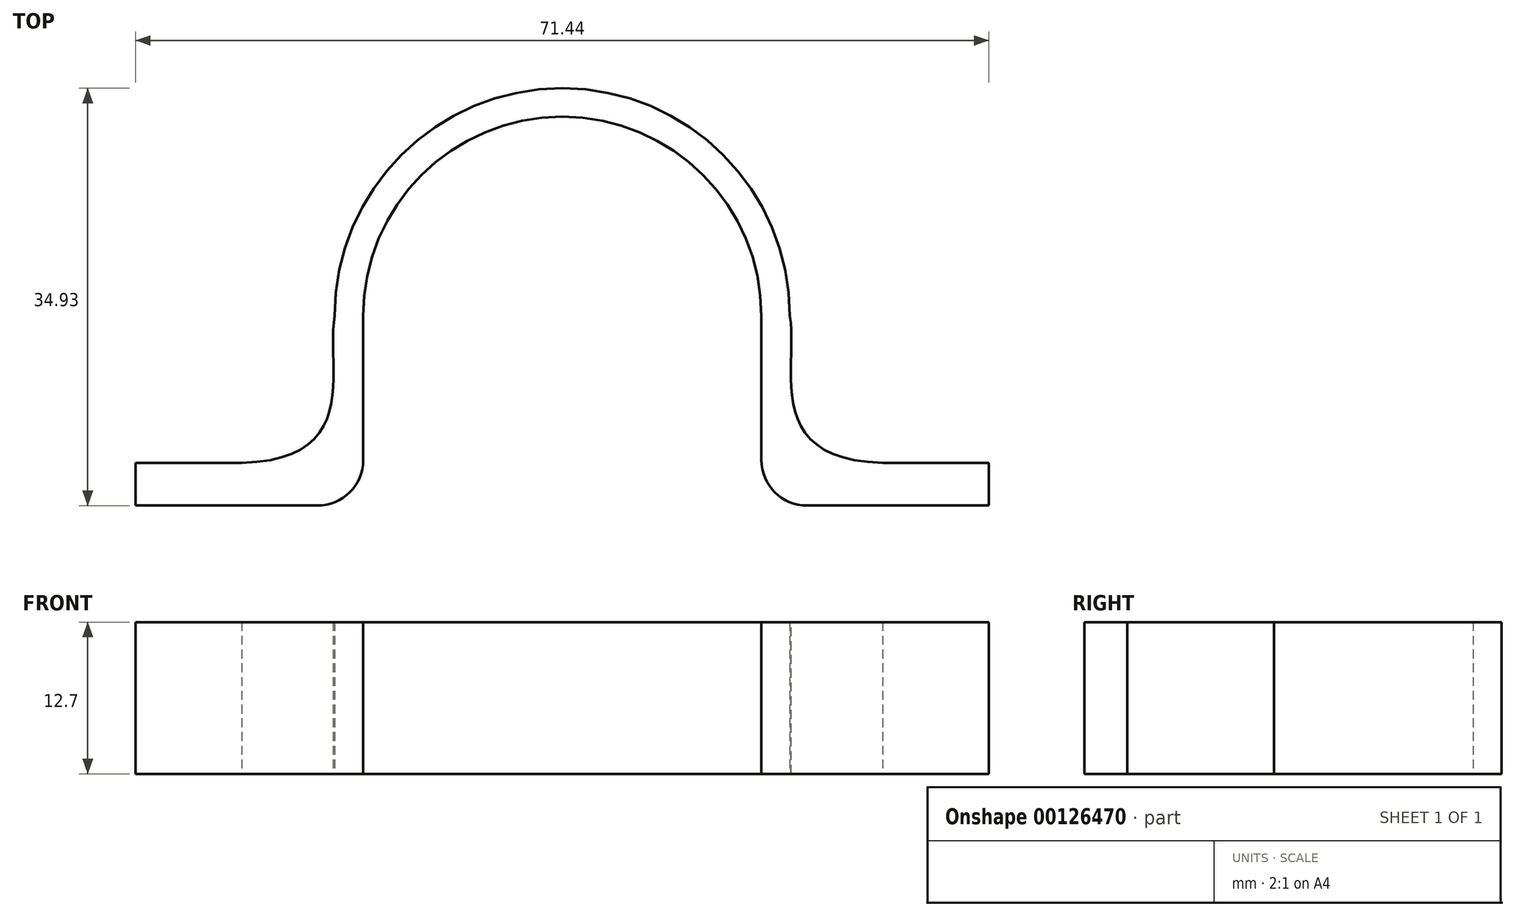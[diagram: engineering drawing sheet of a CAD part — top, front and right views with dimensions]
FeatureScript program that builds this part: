
annotation { "Feature Type Name" : "Feature", "Feature Type Description" : "" }
export const myFeature = defineFeature(function(context is Context, id is Id, definition is map)
    precondition{}
    {
        {
            var Q0;
            Q0=qCreatedBy(makeId("Top.planeOp"),FACE);
            var sketch = newSketch(context, id + "F0", { "sketchPlane" : qUnion([Q0])});
            skCircle(sketch, "E0", {"center": v(0, 0) * mm, "radius": 15.88 * mm, "construction": true});
            skCircle(sketch, "E1", {"center": v(0, 0) * mm, "radius": 16.67 * mm, "construction": true});
            skArc(sketch, "E2", {"start": v(16.67, 0) * mm, "mid": v(11.79, 11.79) * mm, "end": v(0, 16.67) * mm});
            skPoint(sketch, "E3", {"position": v(0, -15.88) * mm});
            skLineSegment(sketch, "E4", {"start": v(16.67, 0) * mm, "end": v(16.67, -12.06) * mm});
            skPoint(sketch, "E5", {"position": v(0, 16.67) * mm});
            skPoint(sketch, "E6", {"position": v(16.67, -15.88) * mm});
            skCircle(sketch, "E7", {"center": v(0, 0) * mm, "radius": 19.05 * mm, "construction": true});
            skLineSegment(sketch, "E8", {"start": v(20.48, -15.88) * mm, "end": v(35.72, -15.88) * mm});
            skArc(sketch, "E9.filletArc", {"start": v(16.67, -12.06) * mm, "mid": v(17.78, -14.76) * mm, "end": v(20.48, -15.87) * mm});
            skPoint(sketch, "E10", {"position": v(0, 19.05) * mm});
            skArc(sketch, "E11", {"start": v(19.05, 0) * mm, "mid": v(13.47, 13.47) * mm, "end": v(0, 19.05) * mm});
            skLineSegment(sketch, "E12", {"start": v(26.82, -12.3) * mm, "end": v(35.72, -12.3) * mm});
            skLineSegment(sketch, "E13", {"start": v(35.72, -12.3) * mm, "end": v(35.72, -15.88) * mm});
            skLineSegment(sketch, "E14", {"start": v(0, 0) * mm, "end": v(0, 19.05) * mm, "construction": true});
            skFitSpline(sketch, "E15", {"points": [v(19.05, 0) * mm, v(26.82, -12.3) * mm], "startDerivative": vector(2.27, -12.75) * mm, "endDerivative": vector(30.46, -0.69) * mm});
            skArc(sketch, "E16.MirrorCS", {"start": v(-19.05, 0) * mm, "mid": v(-13.47, 13.47) * mm, "end": v(0, 19.05) * mm});
            skArc(sketch, "E17.MirrorCS", {"start": v(-16.67, 0) * mm, "mid": v(-11.79, 11.79) * mm, "end": v(0, 16.67) * mm});
            skLineSegment(sketch, "E18.MirrorCS", {"start": v(-16.67, 0) * mm, "end": v(-16.67, -12.06) * mm});
            skFitSpline(sketch, "E19.MirrorCS", {"points": [v(-19.05, 0) * mm, v(-26.82, -12.3) * mm], "startDerivative": vector(-2.27, -12.75) * mm, "endDerivative": vector(-30.46, -0.69) * mm});
            skLineSegment(sketch, "E20.MirrorCS", {"start": v(-26.82, -12.3) * mm, "end": v(-35.72, -12.3) * mm});
            skLineSegment(sketch, "E21.MirrorCS", {"start": v(-35.72, -12.3) * mm, "end": v(-35.72, -15.88) * mm});
            skLineSegment(sketch, "E22.MirrorCS", {"start": v(-20.48, -15.88) * mm, "end": v(-35.72, -15.88) * mm});
            skArc(sketch, "E23.MirrorCS", {"start": v(-16.67, -12.06) * mm, "mid": v(-17.78, -14.76) * mm, "end": v(-20.48, -15.87) * mm});
            skSolve(sketch);
        }
        {
            var Q0;
            Q0=makeQuery(id+"F0.imprint","IMPRINT",FACE,{"disambiguationData":[TD([[makeQuery(id+"F0.imprint","IMPRINT",EDGE,{"derivedFrom":sQuery(id+"F0.wireOp",EDGE,"E2")}),-1.0]])]});
            extrude(context, id + "F1", {"entities" : qUnion([Q0]), "depth" : 12.7 * mm});
        }
    });
